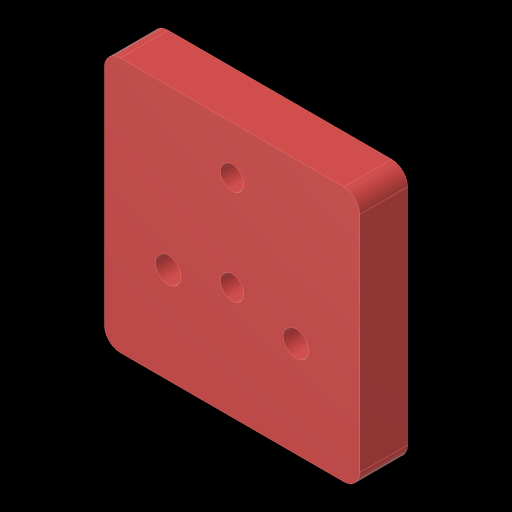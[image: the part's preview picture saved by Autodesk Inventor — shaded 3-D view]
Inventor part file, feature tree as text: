
AUTODESK INVENTOR PART (.ipt)
format: ipt  version: 2023.3 (Build 273359000, 359)  size: 199,680 bytes
history: native  units: in
note: dims shown in document units (in); Inventor stores cm internally (conversion verified against a paired STEP export)
features: hole x2, sketch x1, extrude x1, fillet x1
ambient origin geometry x8: Origin, YZ Plane, XZ Plane, XY Plane, X Axis, Y Axis, Z Axis, Center Point
bodies: Solid1 (feature_tree)
feature tree (5):
  sketch  "Sketch1"  dims[d0=2.0in d1=2.0in d3=0.7447in d4=0.375in d6=0.375in d7=0.0in d8=0.201in d9=0.75in d10=0.375in d11=0.19in d12=0.5635in d13=1.0in d14=0.8108in d15=0.185in d16=0.75in d17=0.225in d18=0.25in d19=0.5635in d20=1.0in d21=0.8108in d22=0.125in d23=1.0in d24=0.75in]
  extrude  "Extrusion1"  Depth=2.0in
  hole  "Hole1"  [1 undecoded]
  hole  "Hole2"  [1 undecoded]
  fillet  "Fillet1"  Radius=0.375in
note: 2 required parameter values undecoded (feature->parameter linkage not recoverable at this tier; creation-order binding heuristic only, values carry confidence <= 0.55)
